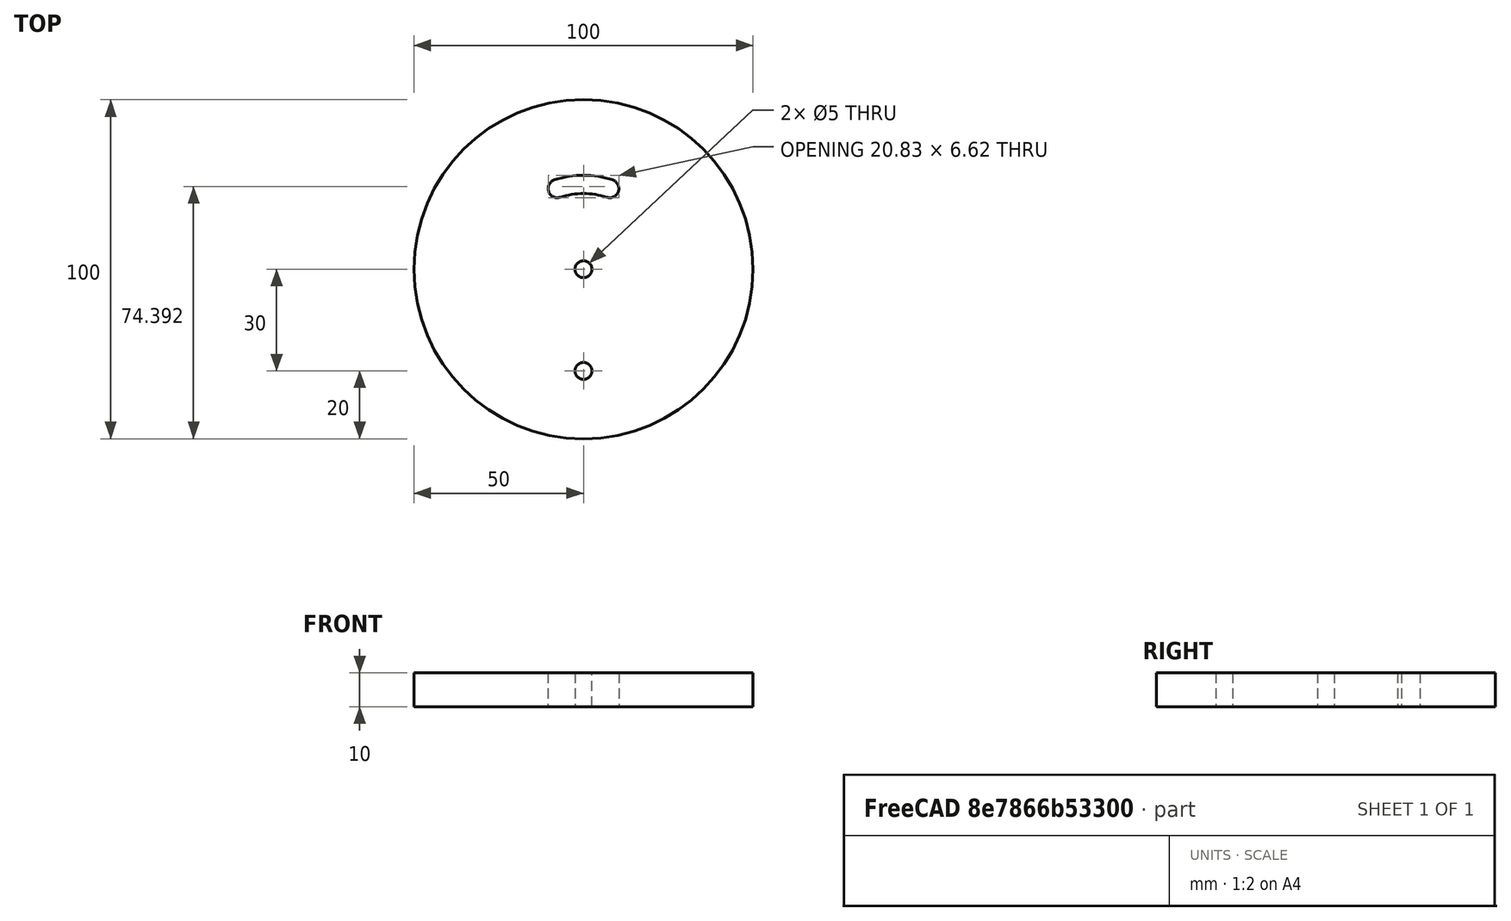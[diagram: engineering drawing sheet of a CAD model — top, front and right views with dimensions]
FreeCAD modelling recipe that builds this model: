
FCSTD DOCUMENT  (FreeCAD 0.22R38467 (Git))
Label: Tab Disc
objects: Sketcher::SketchObject×2, Part::Extrusion×1, PartDesign::CoordinateSystem×1, PartDesign::Line×1, App::Part×1
note: 7 computed .brp shape members not serialized (recipe doc carries the construction recipe); baked Part::Feature solids carry a one-line shape summary decoded from their .brp

FEATURE [Sketcher::SketchObject] Sketch  label="Master Sketch"
  ArcFitTolerance = 1e-06
  FullyConstrained = false
  MakeInternals = false
  sketch-geometry (42):
    g0: Circle CenterX=0 CenterY=0 CenterZ=0 NormalX=0 NormalY=0 NormalZ=1 AngleXU=0 Radius=50
    g1: LineSegment [constr] StartX=0 StartY=0 StartZ=0 EndX=-15.4508 EndY=-47.5528 EndZ=0
    g2: LineSegment [constr] StartX=0 StartY=0 StartZ=0 EndX=15.4508 EndY=-47.5528 EndZ=0
    g3: LineSegment StartX=5 StartY=-14.9956 StartZ=0 EndX=5.01587 EndY=-32.9956 EndZ=0
    g4: LineSegment StartX=-4.99559 StartY=-20.0044 StartZ=0 EndX=-4.98413 EndY=-33.0044 EndZ=0
    g5: ArcOfCircle [constr] CenterX=0 CenterY=-15 CenterZ=0 NormalX=0 NormalY=0 NormalZ=1 AngleXU=0 Radius=15 StartAngle=4.08407 EndAngle=5.34071
    g6: Circle CenterX=0.0132264 CenterY=-30 CenterZ=0 NormalX=0 NormalY=0 NormalZ=1 AngleXU=0 Radius=2.5
    g7: Circle CenterX=0 CenterY=-15 CenterZ=0 NormalX=0 NormalY=0 NormalZ=1 AngleXU=0 Radius=2.5
    g8: ArcOfCircle CenterX=-15 CenterY=-15.0132 CenterZ=0 NormalX=0 NormalY=0 NormalZ=1 AngleXU=0 Radius=5 StartAngle=1.57168 EndAngle=4.71327
    g9: LineSegment StartX=-4.99559 StartY=-20.0044 StartZ=0 EndX=-14.9956 EndY=-20.0132 EndZ=0
    g10: LineSegment StartX=-0.00440879 StartY=-10 StartZ=0 EndX=-15.0044 EndY=-10.0132 EndZ=0
    g11: ArcOfCircle CenterX=0 CenterY=-15 CenterZ=0 NormalX=0 NormalY=0 NormalZ=1 AngleXU=0 Radius=5 StartAngle=0.000881758 EndAngle=1.57168
    g12: ArcOfCircle CenterX=0.0158716 CenterY=-33 CenterZ=0 NormalX=0 NormalY=0 NormalZ=1 AngleXU=0 Radius=5 StartAngle=3.14247 EndAngle=6.28407
    g13: ArcOfCircle CenterX=0.0158716 CenterY=-33 CenterZ=0 NormalX=0 NormalY=0 NormalZ=1 AngleXU=0 Radius=2.7 StartAngle=3.14247 EndAngle=6.28407
    g14: ArcOfCircle CenterX=0.0132264 CenterY=-30 CenterZ=0 NormalX=0 NormalY=0 NormalZ=1 AngleXU=0 Radius=2.7 StartAngle=0.000881758 EndAngle=3.14247
    g15: LineSegment [constr] StartX=-2.68413 StartY=-33.0024 StartZ=0 EndX=-2.68677 EndY=-30.0024 EndZ=0
    g16: LineSegment StartX=2.71587 StartY=-32.9976 StartZ=0 EndX=2.71323 EndY=-29.9976 EndZ=0
    g17: LineSegment [constr] StartX=0 StartY=-15 StartZ=0 EndX=0.0308615 EndY=-50 EndZ=0
    g18: Circle CenterX=-15 CenterY=-15.0132 CenterZ=0 NormalX=0 NormalY=0 NormalZ=1 AngleXU=0 Radius=2.5
    g19: ArcOfCircle CenterX=0 CenterY=0 CenterZ=0 NormalX=0 NormalY=0 NormalZ=1 AngleXU=0 Radius=32.7 StartAngle=1.25664 EndAngle=1.88496
    g20: ArcOfCircle CenterX=-9.27051 CenterY=28.5317 CenterZ=0 NormalX=0 NormalY=0 NormalZ=1 AngleXU=0 Radius=2.7 StartAngle=1.88496 EndAngle=5.02655
    g21: ArcOfCircle CenterX=9.27051 CenterY=28.5317 CenterZ=0 NormalX=0 NormalY=0 NormalZ=1 AngleXU=0 Radius=2.7 StartAngle=4.39823 EndAngle=7.53982
    g22: ArcOfCircle CenterX=0 CenterY=0 CenterZ=0 NormalX=0 NormalY=0 NormalZ=1 AngleXU=0 Radius=27.3 StartAngle=1.25664 EndAngle=1.88496
    g23: LineSegment [constr] StartX=0 StartY=0 StartZ=0 EndX=9.27051 EndY=28.5317 EndZ=0
    g24: LineSegment [constr] StartX=0 StartY=0 StartZ=0 EndX=-9.27051 EndY=28.5317 EndZ=0
    g25: Circle CenterX=0 CenterY=30 CenterZ=0 NormalX=0 NormalY=0 NormalZ=1 AngleXU=0 Radius=2.5
    g26: ArcOfCircle CenterX=-7.45514 CenterY=-31.5066 CenterZ=0 NormalX=0 NormalY=0 NormalZ=1 AngleXU=0 Radius=5 StartAngle=5.97937 EndAngle=6.58876
    g27: ArcOfCircle CenterX=-7.45514 CenterY=-31.5066 CenterZ=0 NormalX=0 NormalY=0 NormalZ=1 AngleXU=0 Radius=4.39478 StartAngle=5.82282 EndAngle=6.74532
    g28: LineSegment [constr] StartX=-2.68545 StartY=-31.5024 StartZ=0 EndX=-4.98545 EndY=-31.5044 EndZ=0
    g29: LineSegment [constr] StartX=-4.98545 StartY=-31.5044 StartZ=0 EndX=-2.68677 EndY=-30.0024 EndZ=0
    g30: LineSegment [constr] StartX=-4.98545 StartY=-31.5044 StartZ=0 EndX=-2.68413 EndY=-33.0024 EndZ=0
    g31: LineSegment StartX=-3.52136 StartY=-29.5471 StartZ=0 EndX=-3.93992 EndY=-29.8206 EndZ=0
    g32: LineSegment StartX=-3.93992 StartY=-29.8206 StartZ=0 EndX=-3.93695 EndY=-33.1863 EndZ=0
    g33: LineSegment StartX=-3.93695 StartY=-33.1863 StartZ=0 EndX=-3.51791 EndY=-33.4591 EndZ=0
    g34: LineSegment [constr] StartX=0 StartY=0 StartZ=0 EndX=-44.8982 EndY=-44.9378 EndZ=0
    g35: LineSegment [constr] StartX=-19.1832 StartY=4.75535 StartZ=0 EndX=7.45294 EndY=-21.8573 EndZ=0
    g36: Circle CenterX=0 CenterY=0 CenterZ=0 NormalX=0 NormalY=0 NormalZ=1 AngleXU=0 Radius=11
    g37: Circle CenterX=0 CenterY=0 CenterZ=0 NormalX=0 NormalY=0 NormalZ=1 AngleXU=0 Radius=30
    g38: Circle [constr] CenterX=-4.94756 CenterY=-4.95193 CenterZ=0 NormalX=0 NormalY=0 NormalZ=1 AngleXU=0 Radius=11
    g39: Circle [constr] CenterX=3.53397 CenterY=3.53709 CenterZ=0 NormalX=0 NormalY=0 NormalZ=1 AngleXU=0 Radius=30
    g40: LineSegment [constr] StartX=-4.98457 StartY=-32.5044 StartZ=0 EndX=-2.41367 EndY=-34.1778 EndZ=0
    g41: LineSegment [constr] StartX=-4.98633 StartY=-30.5044 StartZ=0 EndX=-2.41839 EndY=-28.8264 EndZ=0
  constraints (107):
    c: Diameter(g0) = 100
    c: Coincident(g0,g-1)
    c: Coincident(g1,g0)
    c: PointOnObject(g1,g0)
    c: Coincident(g2,g0)
    c: Symmetric(g2,g1,g-2)
    c: Angle(g1,g2) = 0.628319
    c: PointOnObject(g5,g1)
    c: PointOnObject(g5,g2)
    c: Diameter(g6) = 5
    c: Equal(g7,g6)
    c: Tangent(g8,g9) = 1.5708
    c: Tangent(g8,g10) = -1.5708
    c: Coincident(g9,g4)
    c: Parallel(g3,g4)
    c: Parallel(g9,g10)
    c: Coincident(g11,g7)
    c: Tangent(g11,g3) = 1.5708
    c: Tangent(g11,g10) = -1.5708
    c: Coincident(g7,g5)
    c: PointOnObject(g5,g-2)
    c: DistanceY(g5,g0) = 15
    c: Perpendicular(g9,g4)
    c: Equal(g11,g8)
    c: Radius(g5) = 15
    c: Equal(g12,g8)
    c: Tangent(g12,g3) = 1.5708
    c: Tangent(g12,g4) = -1.5708
    c: Radius(g8) = 5
    c: Distance(g8,g5) = 15
    c: Tangent(g13,g15) = 1.5708
    c: Tangent(g13,g16) = -1.5708
    c: Tangent(g14,g15) = 1.5708
    c: Tangent(g14,g16) = -1.5708
    c: Equal(g13,g14)
    c: Distance(g13,g14) = 3
    c: Radius(g14) = 2.7
    c: Coincident(g17,g5)
    c: PointOnObject(g17,g0)
    c: PointOnObject(g13,g17)
    c: Distance(g14,g5) = 15
    c: PointOnObject(g14,g17)
    c: Coincident(g13,g12)
    c: Distance(g6,g0) = 30
    c: PointOnObject(g6,g17)
    c: Diameter(g18) = 5
    c: Coincident(g18,g8)
    c: Coincident(g19,g22)
    c: Tangent(g22,g21) = 1.5708
    c: Tangent(g22,g20) = 1.5708
    c: Tangent(g19,g21) = -1.5708
    c: Tangent(g19,g20) = -1.5708
    c: Coincident(g19,g0)
    c: Coincident(g23,g0)
    c: Coincident(g23,g21)
    c: Coincident(g24,g0)
    c: Coincident(g24,g20)
    c: Angle(g23,g24) = 0.628319
    c: Distance(g20,g19) = 5.4
    c: Angle(g23,g-2) = 0.314159
    c: Diameter(g25) = 5
    c: PointOnObject(g25,g-2)
    c: Coincident(g26,g14)
    c: Coincident(g26,g13)
    c: Coincident(g27,g26)
    c: Symmetric(g15,g15,g28)
    c: Perpendicular(g15,g28)
    c: Coincident(g29,g14)
    c: Coincident(g30,g29)
    c: Coincident(g30,g13)
    c: Coincident(g27,g31)
    c: Coincident(g31,g32)
    c: Coincident(g32,g33)
    c: Coincident(g33,g27)
    c: Distance(g31) = 0.5
    c: Coincident(g28,g29)
    c: PointOnObject(g28,g4)
    c: Radius(g26) = 5
    c: Equal(g33,g31)
    c: Coincident(g34,g0)
    c: PointOnObject(g8,g34)
    c: Perpendicular(g34,g35)
    c: Diameter(g36) = 22
    c: Coincident(g36,g0)
    c: Diameter(g37) = 60
    c: Coincident(g37,g0)
    c: PointOnObject(g38,g34)
    c: Distance(g38,g0) = 7
    c: PointOnObject(g39,g34)
    c: Distance(g39,g0) = 5
    c: Equal(g39,g37)
    c: Equal(g38,g36)
    c: PointOnObject(g40,g4)
    c: PointOnObject(g40,g13)
    c: PointOnObject(g41,g4)
    c: PointOnObject(g41,g14)
    c: Parallel(g41,g29)
    c: Parallel(g30,g40)
    c: Distance(g40,g28) = 1
    c: Distance(g41,g28) = 1
    c: PointOnObject(g31,g41)
    c: PointOnObject(g32,g40)
    c: PointOnObject(g27,g40)
    c: PointOnObject(g27,g41)
    c: Distance(g41,g31) = 1.25
    c: PointOnObject(g25,g37)
    c: PointOnObject(g21,g37)
FEATURE [Sketcher::SketchObject] Sketch001  label="Top Profile"
  ArcFitTolerance = 1e-06
  FullyConstrained = true
  MakeInternals = false
  sketch-geometry (10):
    g0: Circle CenterX=0 CenterY=0 CenterZ=0 NormalX=0 NormalY=0 NormalZ=1 AngleXU=0 Radius=50
    g1: ArcOfCircle CenterX=-7.72542 CenterY=23.7764 CenterZ=0 NormalX=0 NormalY=0 NormalZ=1 AngleXU=0 Radius=2.7 StartAngle=1.88496 EndAngle=5.02655
    g2: ArcOfCircle CenterX=7.72542 CenterY=23.7764 CenterZ=0 NormalX=0 NormalY=0 NormalZ=1 AngleXU=0 Radius=2.7 StartAngle=4.39823 EndAngle=7.53982
    g3: ArcOfCircle CenterX=0 CenterY=0 CenterZ=0 NormalX=0 NormalY=0 NormalZ=1 AngleXU=0 Radius=27.7 StartAngle=1.25664 EndAngle=1.88496
    g4: ArcOfCircle CenterX=0 CenterY=0 CenterZ=0 NormalX=0 NormalY=0 NormalZ=1 AngleXU=0 Radius=22.3 StartAngle=1.25664 EndAngle=1.88496
    g5: Circle CenterX=0 CenterY=0 CenterZ=0 NormalX=0 NormalY=0 NormalZ=1 AngleXU=0 Radius=2.5
    g6: LineSegment [constr] StartX=0 StartY=0 StartZ=0 EndX=-8.55977 EndY=26.3443 EndZ=0
    g7: LineSegment [constr] StartX=0 StartY=0 StartZ=0 EndX=8.55977 EndY=26.3443 EndZ=0
    g8: Circle CenterX=0 CenterY=-30 CenterZ=0 NormalX=0 NormalY=0 NormalZ=1 AngleXU=0 Radius=2.5
    g9: Circle [constr] CenterX=0 CenterY=0 CenterZ=0 NormalX=0 NormalY=0 NormalZ=1 AngleXU=0 Radius=15
  constraints (27):
    c: Coincident(g0,g-1)
    c: Coincident(g3,g1)
    c: Coincident(g3,g2)
    c: Coincident(g4,g1)
    c: Coincident(g4,g2)
    c: Diameter(g5) = 5
    c: Coincident(g5,g0)
    c: Coincident(g6,g3)
    c: Coincident(g6,g1)
    c: Coincident(g7,g4)
    c: Coincident(g7,g2)
    c: PointOnObject(g2,g7)
    c: PointOnObject(g2,g7)
    c: PointOnObject(g1,g6)
    c: PointOnObject(g1,g6)
    c: Angle(g7,g-2) = 0.314159
    c: Coincident(g3,g0)
    c: Coincident(g4,g0)
    c: Angle(g-2,g6) = 0.314159
    c: Radius(g0) = 50
    c: Diameter(g8) = 5
    c: PointOnObject(g8,g-2)
    c: DistanceY(g8) = -30
    c: Radius(g1) = 2.7
    c: Distance(g1,g0) = 25
    c: Diameter(g9) = 30
    c: Coincident(g9,g0)
FEATURE [Part::Extrusion] Extrude
  Base = -> Sketch001
  Dir = (0,0,1)
  DirMode = 2
  FaceMakerClass = Part::FaceMakerBullseye
  FaceMakerMode = 3
  LengthFwd = 10
  LengthRev = 0
  Solid = true
  Symmetric = false
FEATURE [PartDesign::CoordinateSystem] LCS_Origin  label="Axle AP"
  AttacherType = Attacher::AttachEngine3D
  AttachmentSupport = -> [X_Axis]
  MapMode = 2
FEATURE [PartDesign::Line] HoleAxis_1  label="Control Pin  AP"
  AttacherType = Attacher::AttachEngineLine
  AttachmentSupport = -> [Extrude]
  Length = 7.04534
  MapMode = 19
  Placement = pos=(0,-30,0) rot=(0,0,1;0rad)
  ResizeMode = 1
FEATURE [App::Part] Tab_Disc  label="Tab Disc"
  Group = -> [LCS_Origin,Sketch001,Extrude,HoleAxis_1]
  Origin = -> Origin
